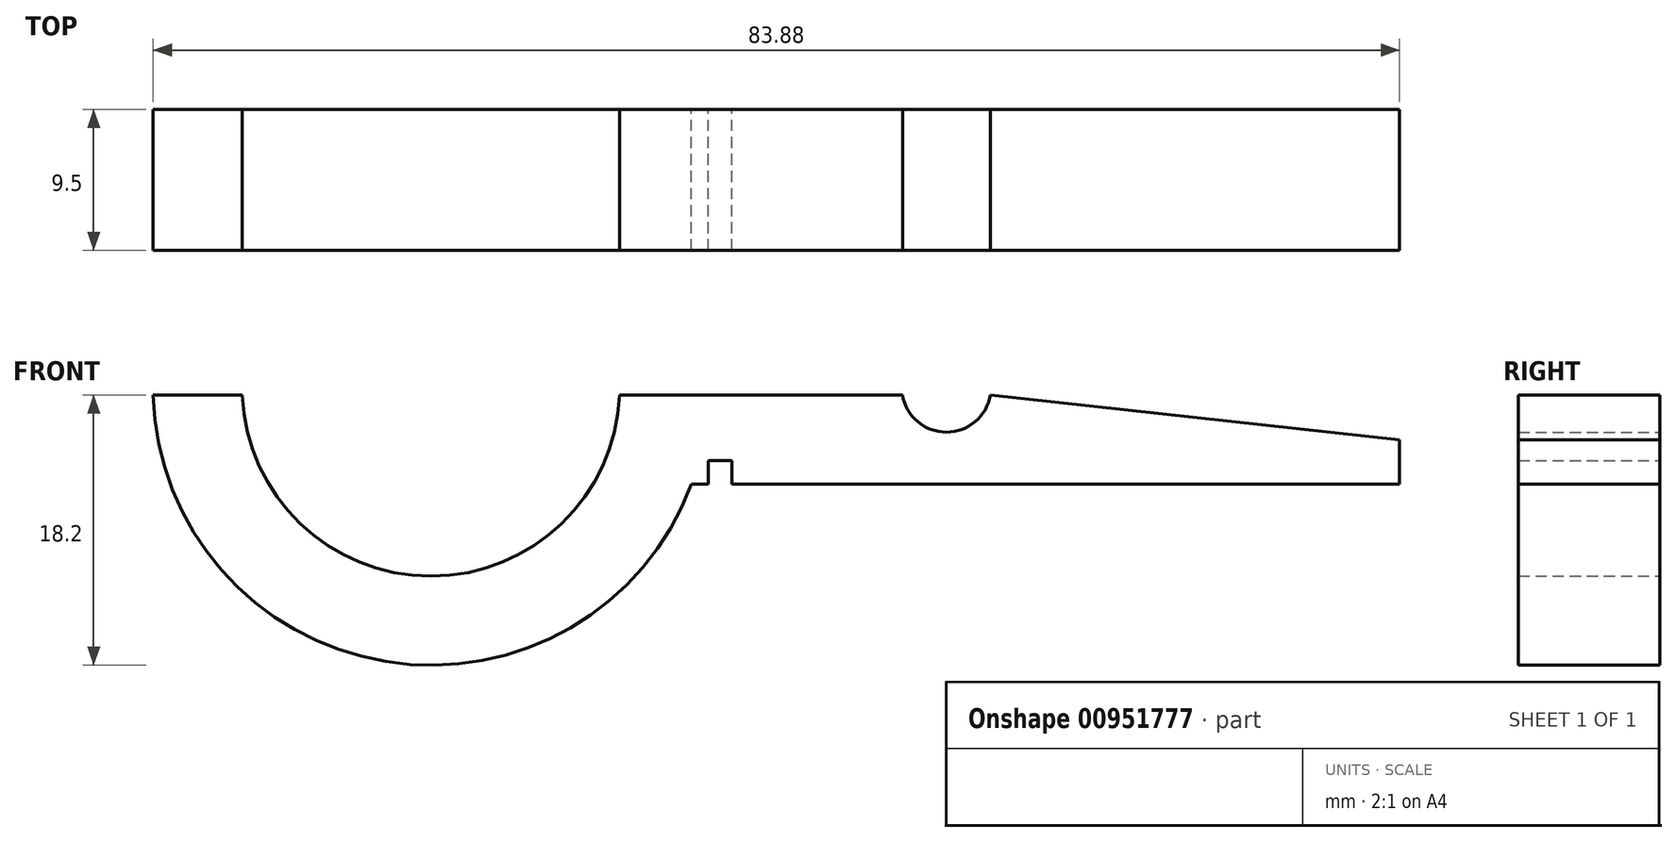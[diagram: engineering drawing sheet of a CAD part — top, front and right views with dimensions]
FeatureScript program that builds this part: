
annotation { "Feature Type Name" : "Feature", "Feature Type Description" : "" }
export const myFeature = defineFeature(function(context is Context, id is Id, definition is map)
    precondition{}
    {
        {
            assignVariable(context, id + "F0", {"name" : "springwidth", "anyValue" : 12});
        }
        {
            var Q0;
            Q0=qCreatedBy(makeId("Front.planeOp"),FACE);
            var sketch = newSketch(context, id + "F1", { "sketchPlane" : qUnion([Q0])});
            skLineSegment(sketch, "E0.right", {"start": v(30.5, -6.5) * mm, "end": v(30.5, -3.5) * mm});
            skLineSegment(sketch, "E1", {"start": v(2.96, -0.5) * mm, "end": v(30.5, -3.5) * mm});
            skLineSegment(sketch, "E2.trimOffspring", {"start": v(-22, -0.5) * mm, "end": v(-17.18, -0.5) * mm});
            skPoint(sketch, "E3.center.orphan", {"position": v(0, 0) * mm});
            skArc(sketch, "E4", {"start": v(-2.96, -0.5) * mm, "mid": v(0, -3) * mm, "end": v(2.96, -0.5) * mm});
            skLineSegment(sketch, "E5.top", {"start": v(-16.03, -4.9) * mm, "end": v(-14.43, -4.9) * mm});
            skLineSegment(sketch, "E5.left", {"start": v(-16.03, -6.5) * mm, "end": v(-16.03, -4.9) * mm});
            skLineSegment(sketch, "E5.right", {"start": v(-14.43, -6.5) * mm, "end": v(-14.43, -4.9) * mm});
            skLineSegment(sketch, "E6.trimOffspring", {"start": v(-14.43, -6.5) * mm, "end": v(30.5, -6.5) * mm});
            skPoint(sketch, "E7", {"position": v(-15.23, -4.9) * mm});
            skLineSegment(sketch, "E8", {"start": v(-2.96, -0.5) * mm, "end": v(2.96, -0.5) * mm, "construction": true});
            skArc(sketch, "E9", {"start": v(-47.38, -0.5) * mm, "mid": v(-34.7, -12.7) * mm, "end": v(-22, -0.5) * mm});
            skLineSegment(sketch, "E10", {"start": v(-17.18, -0.5) * mm, "end": v(-17.16, -0.5) * mm});
            skArc(sketch, "E11", {"start": v(-53.38, -0.5) * mm, "mid": v(-37.75, -18.45) * mm, "end": v(-17.16, -6.5) * mm});
            skLineSegment(sketch, "E12", {"start": v(-16, -0.5) * mm, "end": v(-16, -0.5) * mm});
            skLineSegment(sketch, "E13", {"start": v(-17.16, -0.5) * mm, "end": v(-2.96, -0.5) * mm});
            skLineSegment(sketch, "E14", {"start": v(-17.16, -6.5) * mm, "end": v(-16.03, -6.5) * mm});
            skLineSegment(sketch, "E15", {"start": v(-53.38, -0.5) * mm, "end": v(-47.38, -0.5) * mm});
            skSolve(sketch);
        }
        {
            var Q0;
            Q0=makeQuery(id+"F1.imprint","IMPRINT",FACE,{"disambiguationData":[TD([[makeQuery(id+"F1.imprint","IMPRINT",EDGE,{"derivedFrom":sQuery(id+"F1.wireOp",EDGE,"E0.right")}),1.0]])]});
            extrude(context, id + "F2", {"entities" : qUnion([Q0]), "offsetDistance" : 25 * mm, "depth" : (getVariable(context, 'springwidth') - 2.5) * mm});
        }
    });
